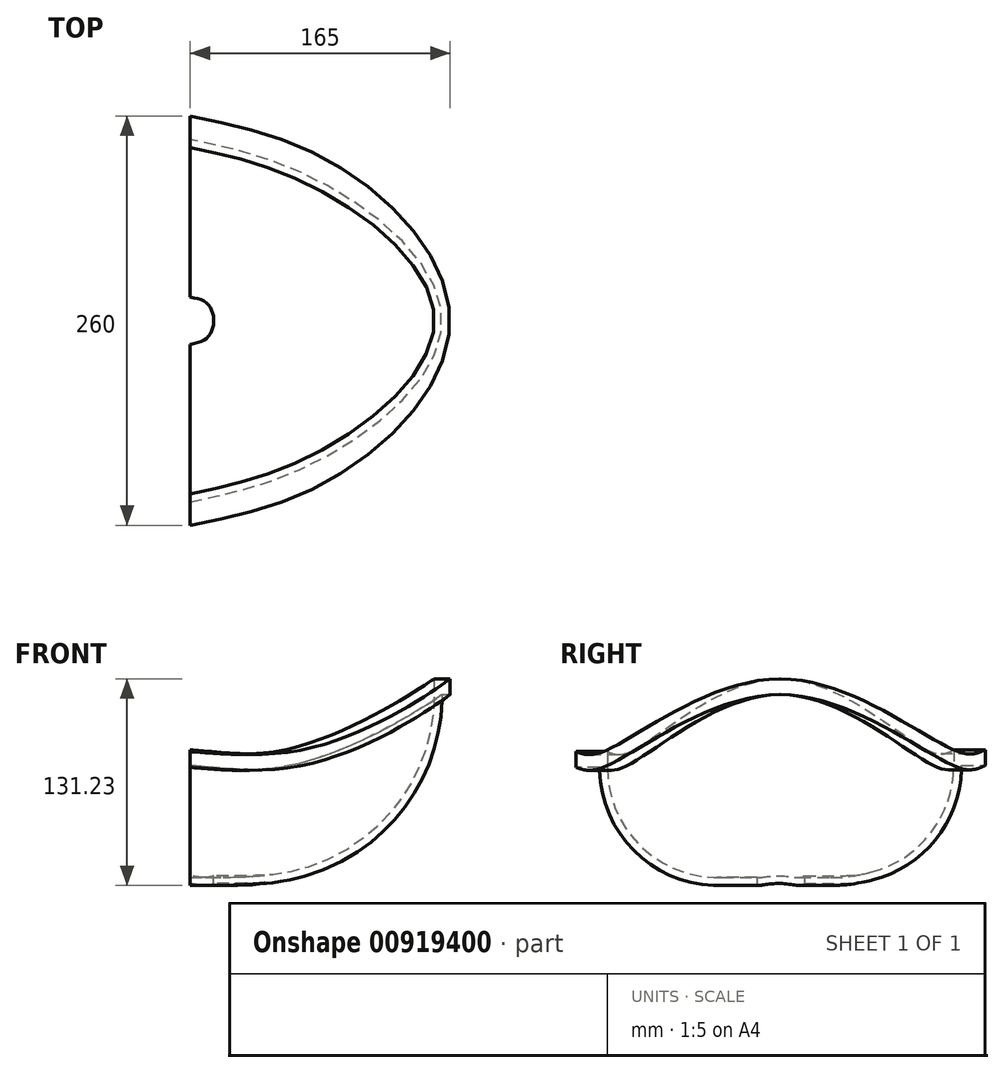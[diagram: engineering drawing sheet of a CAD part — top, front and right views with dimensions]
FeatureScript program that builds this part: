
annotation { "Feature Type Name" : "Feature", "Feature Type Description" : "" }
export const myFeature = defineFeature(function(context is Context, id is Id, definition is map)
    precondition{}
    {
        {
            var Q0;
            Q0=qCreatedBy(makeId("Front.planeOp"),FACE);
            var sketch = newSketch(context, id + "F0", { "sketchPlane" : qUnion([Q0])});
            skLineSegment(sketch, "E0.bottom", {"start": v(15, 5) * mm, "end": v(40, 5) * mm});
            skLineSegment(sketch, "E0.top", {"start": v(15, 0) * mm, "end": v(40, 0) * mm});
            skLineSegment(sketch, "E0.left", {"start": v(15, 5) * mm, "end": v(15, 0) * mm});
            skLineSegment(sketch, "E0.right", {"start": v(40, 5) * mm, "end": v(40, 0) * mm, "construction": true});
            skLineSegment(sketch, "E1.bottom", {"start": v(155, 130) * mm, "end": v(165, 130) * mm});
            skLineSegment(sketch, "E1.top", {"start": v(160, 120) * mm, "end": v(165, 120) * mm});
            skLineSegment(sketch, "E1.left", {"start": v(155, 130) * mm, "end": v(155, 120) * mm});
            skLineSegment(sketch, "E1.right", {"start": v(165, 130) * mm, "end": v(165, 120) * mm});
            skArc(sketch, "E2", {"start": v(40, 0) * mm, "mid": v(124.85, 35.15) * mm, "end": v(160, 120) * mm});
            skArc(sketch, "E3", {"start": v(40, 5) * mm, "mid": v(121.32, 38.68) * mm, "end": v(155, 120) * mm});
            skLineSegment(sketch, "E4", {"start": v(0, 0) * mm, "end": v(0, 75) * mm, "construction": true});
            skSolve(sketch);
        }
        {
            var Q0;
            Q0=sQuery(id+"F0.wireOp",EDGE,"E4");
            cPlane(context, id + "F1", {"entities" : qUnion([Q0]), "cplaneType" : CPlaneType.LINE_ANGLE, "offset" : 25 * mm, "angle" : 30 * degree, "oppositeDirection" : true, "width" : 150 * mm, "height" : 150 * mm});
        }
        {
            var Q0;
            Q0=qCreatedBy(id+"F1.planeOp",FACE);
            var sketch = newSketch(context, id + "F2", { "sketchPlane" : qUnion([Q0])});
            skLineSegment(sketch, "E5.bottom", {"start": v(15, 3.85) * mm, "end": v(40, 3.85) * mm});
            skLineSegment(sketch, "E5.top", {"start": v(15, -1.15) * mm, "end": v(40, -1.15) * mm});
            skLineSegment(sketch, "E5.left", {"start": v(15, 3.85) * mm, "end": v(15, -1.15) * mm});
            skLineSegment(sketch, "E5.right", {"start": v(40, 3.85) * mm, "end": v(40, -1.15) * mm, "construction": true});
            skLineSegment(sketch, "E6.bottom", {"start": v(110, 83.85) * mm, "end": v(130, 83.85) * mm});
            skLineSegment(sketch, "E6.top", {"start": v(115, 73.85) * mm, "end": v(130, 73.85) * mm});
            skLineSegment(sketch, "E6.left", {"start": v(110, 83.85) * mm, "end": v(110, 73.85) * mm});
            skLineSegment(sketch, "E6.right", {"start": v(130, 83.85) * mm, "end": v(130, 73.85) * mm});
            skArc(sketch, "E7", {"start": v(40, -1.15) * mm, "mid": v(93.03, 20.81) * mm, "end": v(115, 73.85) * mm});
            skArc(sketch, "E8", {"start": v(40, 3.85) * mm, "mid": v(89.5, 24.35) * mm, "end": v(110, 73.85) * mm});
            skLineSegment(sketch, "E9", {"start": v(0, 0) * mm, "end": v(0, 75) * mm, "construction": true});
            skSolve(sketch);
        }
        {
            var Q0;
            Q0=sQuery(id+"F0.wireOp",EDGE,"E4");
            cPlane(context, id + "F3", {"entities" : qUnion([Q0]), "cplaneType" : CPlaneType.LINE_ANGLE, "offset" : 25 * mm, "angle" : 150 * degree, "oppositeDirection" : true, "width" : 150 * mm, "height" : 150 * mm});
        }
        {
            var Q0;
            Q0=qCreatedBy(id+"F3.planeOp",FACE);
            var sketch = newSketch(context, id + "F4", { "sketchPlane" : qUnion([Q0])});
            skLineSegment(sketch, "E10.bottom", {"start": v(15, 3.85) * mm, "end": v(40, 3.85) * mm});
            skLineSegment(sketch, "E10.top", {"start": v(15, -1.15) * mm, "end": v(40, -1.15) * mm});
            skLineSegment(sketch, "E10.left", {"start": v(15, 3.85) * mm, "end": v(15, -1.15) * mm});
            skLineSegment(sketch, "E10.right", {"start": v(40, 3.85) * mm, "end": v(40, -1.15) * mm, "construction": true});
            skLineSegment(sketch, "E11.bottom", {"start": v(110, 83.85) * mm, "end": v(130, 83.85) * mm});
            skLineSegment(sketch, "E11.top", {"start": v(115, 73.85) * mm, "end": v(130, 73.85) * mm});
            skLineSegment(sketch, "E11.left", {"start": v(110, 83.85) * mm, "end": v(110, 73.85) * mm});
            skLineSegment(sketch, "E11.right", {"start": v(130, 83.85) * mm, "end": v(130, 73.85) * mm});
            skArc(sketch, "E12", {"start": v(40, -1.15) * mm, "mid": v(93.03, 20.81) * mm, "end": v(115, 73.85) * mm});
            skArc(sketch, "E13", {"start": v(40, 3.85) * mm, "mid": v(89.5, 24.35) * mm, "end": v(110, 73.85) * mm});
            skLineSegment(sketch, "E14", {"start": v(0, 0) * mm, "end": v(0, 75) * mm, "construction": true});
            skSolve(sketch);
        }
        {
            var Q0;
            Q0=qCreatedBy(makeId("Right.planeOp"),FACE);
            var sketch = newSketch(context, id + "F5", { "sketchPlane" : qUnion([Q0])});
            skLineSegment(sketch, "E15.bottom", {"start": v(15, 5) * mm, "end": v(40, 5) * mm});
            skLineSegment(sketch, "E15.top", {"start": v(15, 0) * mm, "end": v(40, 0) * mm});
            skLineSegment(sketch, "E15.left", {"start": v(15, 5) * mm, "end": v(15, 0) * mm});
            skLineSegment(sketch, "E15.right", {"start": v(40, 5) * mm, "end": v(40, 0) * mm, "construction": true});
            skLineSegment(sketch, "E16.bottom", {"start": v(110, 85) * mm, "end": v(130, 85) * mm});
            skLineSegment(sketch, "E16.top", {"start": v(115, 75) * mm, "end": v(130, 75) * mm});
            skLineSegment(sketch, "E16.left", {"start": v(110, 85) * mm, "end": v(110, 75) * mm});
            skLineSegment(sketch, "E16.right", {"start": v(130, 85) * mm, "end": v(130, 75) * mm});
            skArc(sketch, "E17", {"start": v(40, 0) * mm, "mid": v(93.03, 21.97) * mm, "end": v(115, 75) * mm});
            skArc(sketch, "E18", {"start": v(40, 5) * mm, "mid": v(89.5, 25.5) * mm, "end": v(110, 75) * mm});
            skLineSegment(sketch, "E19", {"start": v(0, 0) * mm, "end": v(0, 75) * mm, "construction": true});
            skSolve(sketch);
        }
        {
            var Q0;
            Q0=sQuery(id+"F5.wireOp",EDGE,"E19");
            cPlane(context, id + "F6", {"entities" : qUnion([Q0]), "cplaneType" : CPlaneType.LINE_ANGLE, "offset" : 25 * mm, "angle" : 180 * degree, "width" : 150 * mm, "height" : 150 * mm});
        }
        {
            var Q0;
            Q0=qCreatedBy(id+"F6.planeOp",FACE);
            var sketch = newSketch(context, id + "F7", { "sketchPlane" : qUnion([Q0])});
            skLineSegment(sketch, "E20.bottom", {"start": v(15, 3.85) * mm, "end": v(40, 3.85) * mm});
            skLineSegment(sketch, "E20.top", {"start": v(15, -1.15) * mm, "end": v(40, -1.15) * mm});
            skLineSegment(sketch, "E20.left", {"start": v(15, 3.85) * mm, "end": v(15, -1.15) * mm});
            skLineSegment(sketch, "E20.right", {"start": v(40, 3.85) * mm, "end": v(40, -1.15) * mm, "construction": true});
            skLineSegment(sketch, "E21.bottom", {"start": v(110, 83.85) * mm, "end": v(130, 83.85) * mm});
            skLineSegment(sketch, "E21.top", {"start": v(115, 73.85) * mm, "end": v(130, 73.85) * mm});
            skLineSegment(sketch, "E21.left", {"start": v(110, 83.85) * mm, "end": v(110, 73.85) * mm});
            skLineSegment(sketch, "E21.right", {"start": v(130, 83.85) * mm, "end": v(130, 73.85) * mm});
            skArc(sketch, "E22", {"start": v(40, -1.15) * mm, "mid": v(93.03, 20.81) * mm, "end": v(115, 73.85) * mm});
            skArc(sketch, "E23", {"start": v(40, 3.85) * mm, "mid": v(89.5, 24.35) * mm, "end": v(110, 73.85) * mm});
            skLineSegment(sketch, "E24", {"start": v(0, 0) * mm, "end": v(0, 75) * mm, "construction": true});
            skSolve(sketch);
        }
        {
            var Q0;
            Q0=makeQuery(id+"F7.imprint","IMPRINT",FACE,{"disambiguationData":[TD([[makeQuery(id+"F7.imprint","IMPRINT",EDGE,{"derivedFrom":sQuery(id+"F7.wireOp",EDGE,"E20.bottom")}),-1.0]])]});
            var Q1;
            Q1=makeQuery(id+"F4.imprint","IMPRINT",FACE,{"disambiguationData":[TD([[makeQuery(id+"F4.imprint","IMPRINT",EDGE,{"derivedFrom":sQuery(id+"F4.wireOp",EDGE,"E10.bottom")}),-1.0]])]});
            var Q2;
            Q2=makeQuery(id+"F0.imprint","IMPRINT",FACE,{"disambiguationData":[TD([[makeQuery(id+"F0.imprint","IMPRINT",EDGE,{"derivedFrom":sQuery(id+"F0.wireOp",EDGE,"E0.bottom")}),-1.0]])]});
            var Q3;
            Q3=makeQuery(id+"F2.imprint","IMPRINT",FACE,{"disambiguationData":[TD([[makeQuery(id+"F2.imprint","IMPRINT",EDGE,{"derivedFrom":sQuery(id+"F2.wireOp",EDGE,"E5.bottom")}),-1.0]])]});
            var Q4;
            Q4=makeQuery(id+"F5.imprint","IMPRINT",FACE,{"disambiguationData":[TD([[makeQuery(id+"F5.imprint","IMPRINT",EDGE,{"derivedFrom":sQuery(id+"F5.wireOp",EDGE,"E15.bottom")}),-1.0]])]});
            loft(context, id + "F8", {"sheetProfilesArray" : [{ "sheetProfileEntities" : qUnion([Q0]) }, { "sheetProfileEntities" : qUnion([Q1]) }, { "sheetProfileEntities" : qUnion([Q2]) }, { "sheetProfileEntities" : qUnion([Q3]) }, { "sheetProfileEntities" : qUnion([Q4]) }]});
        }
    });
